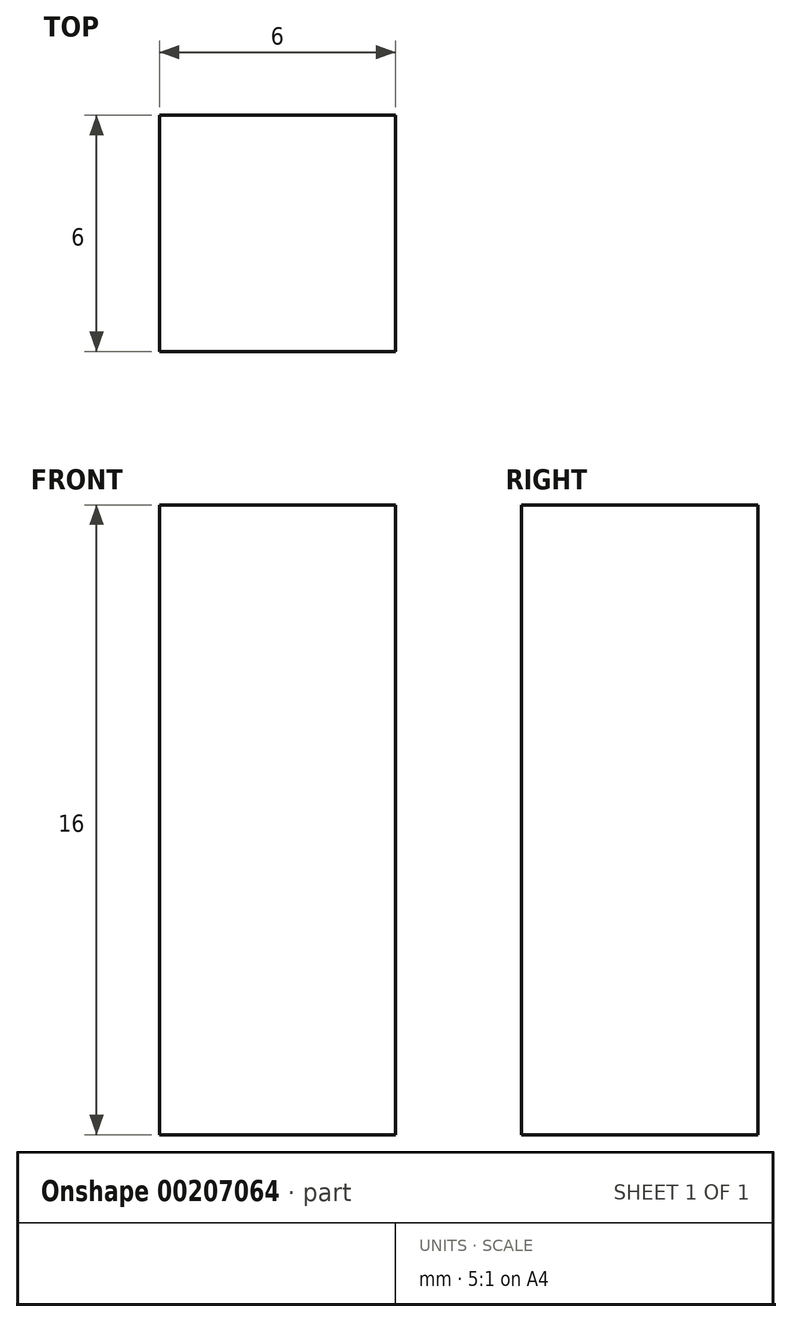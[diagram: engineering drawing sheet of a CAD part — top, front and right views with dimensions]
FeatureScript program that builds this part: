
annotation { "Feature Type Name" : "Feature", "Feature Type Description" : "" }
export const myFeature = defineFeature(function(context is Context, id is Id, definition is map)
    precondition{}
    {
        {
            var Q0;
            Q0=qCreatedBy(makeId("Top.planeOp"),FACE);
            var sketch = newSketch(context, id + "F0", { "sketchPlane" : qUnion([Q0])});
            skLineSegment(sketch, "E0.bottom", {"start": v(3, -3) * mm, "end": v(-3, -3) * mm});
            skLineSegment(sketch, "E0.top", {"start": v(3, 3) * mm, "end": v(-3, 3) * mm});
            skLineSegment(sketch, "E0.left", {"start": v(3, -3) * mm, "end": v(3, 3) * mm});
            skLineSegment(sketch, "E0.right", {"start": v(-3, -3) * mm, "end": v(-3, 3) * mm});
            skPoint(sketch, "E0.middle", {"position": v(0, 0) * mm});
            skSolve(sketch);
        }
        {
            var Q0;
            Q0=makeQuery(id+"F0.imprint","IMPRINT",FACE,{"disambiguationData":[TD([[makeQuery(id+"F0.imprint","IMPRINT",EDGE,{"derivedFrom":sQuery(id+"F0.wireOp",EDGE,"E0.bottom")}),-1.0]])]});
            extrude(context, id + "F1", {"entities" : qUnion([Q0]), "depth" : 16 * mm, "offsetDistance" : 25 * mm});
        }
    });
